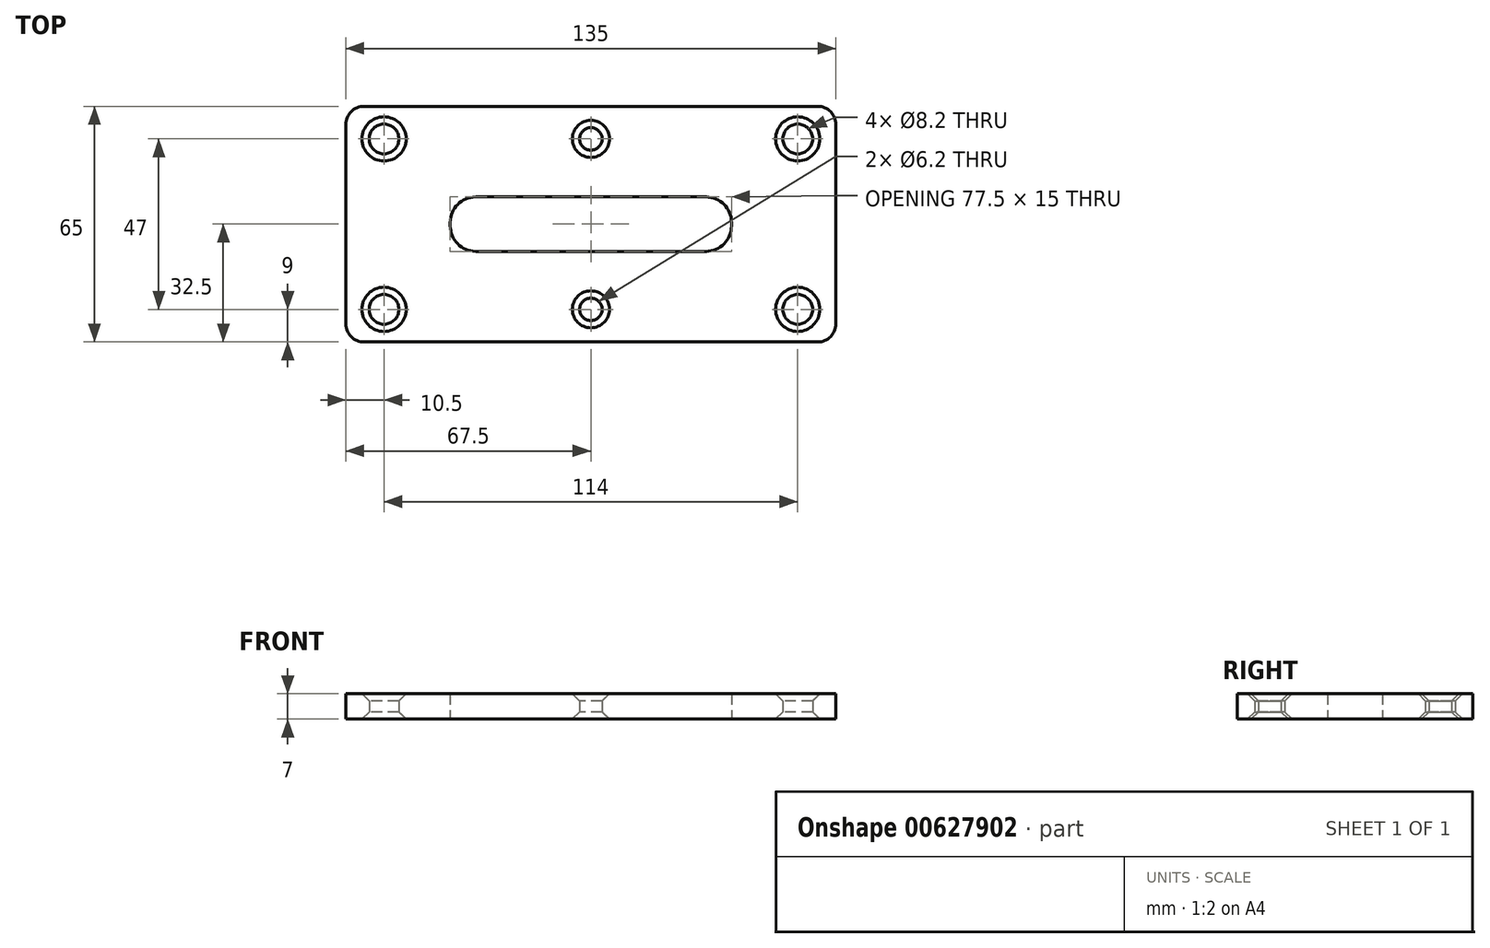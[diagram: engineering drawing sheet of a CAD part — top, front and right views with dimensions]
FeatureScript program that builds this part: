
annotation { "Feature Type Name" : "Feature", "Feature Type Description" : "" }
export const myFeature = defineFeature(function(context is Context, id is Id, definition is map)
    precondition{}
    {
        {
            var Q0;
            Q0=qCreatedBy(makeId("Top.planeOp"),FACE);
            var sketch = newSketch(context, id + "F0", { "sketchPlane" : qUnion([Q0])});
            skLineSegment(sketch, "E0.bottom", {"start": v(62.5, 32.5) * mm, "end": v(-62.5, 32.5) * mm});
            skLineSegment(sketch, "E0.top", {"start": v(62.5, -32.5) * mm, "end": v(-62.5, -32.5) * mm});
            skLineSegment(sketch, "E0.left", {"start": v(67.5, 27.5) * mm, "end": v(67.5, -27.5) * mm});
            skLineSegment(sketch, "E0.right", {"start": v(-67.5, 27.5) * mm, "end": v(-67.5, -27.5) * mm});
            skPoint(sketch, "E0.middle", {"position": v(0, 0) * mm});
            skLineSegment(sketch, "E1.bottom", {"start": v(31.75, 7.5) * mm, "end": v(-31.75, 7.5) * mm});
            skLineSegment(sketch, "E1.top", {"start": v(31.75, -7.5) * mm, "end": v(-31.75, -7.5) * mm});
            skLineSegment(sketch, "E1.left", {"start": v(38.75, 0.5) * mm, "end": v(38.75, -0.5) * mm});
            skLineSegment(sketch, "E1.right", {"start": v(-38.75, 0.5) * mm, "end": v(-38.75, -0.5) * mm});
            skPoint(sketch, "E2.visualSharp", {"position": v(-38.75, 7.5) * mm});
            skArc(sketch, "E2.filletArc", {"start": v(-31.75, 7.5) * mm, "mid": v(-36.7, 5.45) * mm, "end": v(-38.75, 0.5) * mm});
            skPoint(sketch, "E3.visualSharp", {"position": v(-38.75, -7.5) * mm});
            skArc(sketch, "E3.filletArc", {"start": v(-38.75, -0.5) * mm, "mid": v(-36.7, -5.45) * mm, "end": v(-31.75, -7.5) * mm});
            skPoint(sketch, "E4.visualSharp", {"position": v(38.75, 7.5) * mm});
            skArc(sketch, "E4.filletArc", {"start": v(38.75, 0.5) * mm, "mid": v(36.7, 5.45) * mm, "end": v(31.75, 7.5) * mm});
            skPoint(sketch, "E5.visualSharp", {"position": v(38.75, -7.5) * mm});
            skArc(sketch, "E5.filletArc", {"start": v(31.75, -7.5) * mm, "mid": v(36.7, -5.45) * mm, "end": v(38.75, -0.5) * mm});
            skPoint(sketch, "E6.visualSharp", {"position": v(-67.5, 32.5) * mm});
            skArc(sketch, "E6.filletArc", {"start": v(-62.5, 32.5) * mm, "mid": v(-66.04, 31.04) * mm, "end": v(-67.5, 27.5) * mm});
            skPoint(sketch, "E7.visualSharp", {"position": v(-67.5, -32.5) * mm});
            skArc(sketch, "E7.filletArc", {"start": v(-67.5, -27.5) * mm, "mid": v(-66.04, -31.04) * mm, "end": v(-62.5, -32.5) * mm});
            skPoint(sketch, "E8.visualSharp", {"position": v(67.5, 32.5) * mm});
            skArc(sketch, "E8.filletArc", {"start": v(67.5, 27.5) * mm, "mid": v(66.04, 31.04) * mm, "end": v(62.5, 32.5) * mm});
            skPoint(sketch, "E9.visualSharp", {"position": v(67.5, -32.5) * mm});
            skArc(sketch, "E9.filletArc", {"start": v(62.5, -32.5) * mm, "mid": v(66.04, -31.04) * mm, "end": v(67.5, -27.5) * mm});
            skLineSegment(sketch, "E10.bottom", {"start": v(-57, 23.5) * mm, "end": v(57, 23.5) * mm, "construction": true});
            skLineSegment(sketch, "E10.top", {"start": v(-57, -23.5) * mm, "end": v(57, -23.5) * mm, "construction": true});
            skLineSegment(sketch, "E10.left", {"start": v(-57, 23.5) * mm, "end": v(-57, -23.5) * mm, "construction": true});
            skLineSegment(sketch, "E10.right", {"start": v(57, 23.5) * mm, "end": v(57, -23.5) * mm, "construction": true});
            skCircle(sketch, "E11", {"center": v(57, 23.5) * mm, "radius": 4.1 * mm});
            skCircle(sketch, "E12", {"center": v(57, -23.5) * mm, "radius": 4.1 * mm});
            skCircle(sketch, "E13", {"center": v(-57, -23.5) * mm, "radius": 4.1 * mm});
            skCircle(sketch, "E14", {"center": v(-57, 23.5) * mm, "radius": 4.1 * mm});
            skCircle(sketch, "E15", {"center": v(0, 23.5) * mm, "radius": 3.1 * mm});
            skCircle(sketch, "E16", {"center": v(0, -23.5) * mm, "radius": 3.1 * mm});
            skLineSegment(sketch, "E17", {"start": v(0, 36.6) * mm, "end": v(0, -44.9) * mm, "construction": true});
            skLineSegment(sketch, "E18", {"start": v(-80.9, 0) * mm, "end": v(96.11, 0) * mm, "construction": true});
            skSolve(sketch);
        }
        {
            var Q0;
            Q0=makeQuery(id+"F0.imprint","IMPRINT",FACE,{"disambiguationData":[TD([[makeQuery(id+"F0.imprint","IMPRINT",EDGE,{"derivedFrom":sQuery(id+"F0.wireOp",EDGE,"E0.bottom")}),1.0]])]});
            extrude(context, id + "F1", {"entities" : qUnion([Q0]), "depth" : 7 * mm, "offsetDistance" : 25 * mm});
        }
        {
            var Q0;
            Q0=makeQuery(id+"F1.opExtrude","SWEPT_FACE",FACE,{"disambiguationData":[OSD([sQuery(id+"F0.wireOp",EDGE,"E13")])]});
            var Q1;
            Q1=makeQuery(id+"F1.opExtrude","SWEPT_FACE",FACE,{"disambiguationData":[OSD([sQuery(id+"F0.wireOp",EDGE,"E14")])]});
            var Q2;
            Q2=makeQuery(id+"F1.opExtrude","SWEPT_FACE",FACE,{"disambiguationData":[OSD([sQuery(id+"F0.wireOp",EDGE,"E15")])]});
            var Q3;
            Q3=makeQuery(id+"F1.opExtrude","SWEPT_FACE",FACE,{"disambiguationData":[OSD([sQuery(id+"F0.wireOp",EDGE,"E11")])]});
            var Q4;
            Q4=makeQuery(id+"F1.opExtrude","SWEPT_FACE",FACE,{"disambiguationData":[OSD([sQuery(id+"F0.wireOp",EDGE,"E12")])]});
            var Q5;
            Q5=makeQuery(id+"F1.opExtrude","SWEPT_FACE",FACE,{"disambiguationData":[OSD([sQuery(id+"F0.wireOp",EDGE,"E16")])]});
            chamfer(context, id + "F2", {"entities" : qUnion([Q0, Q1, Q2, Q3, Q4, Q5]), "width" : 2 * mm, "tangentPropagation" : true});
        }
    });
